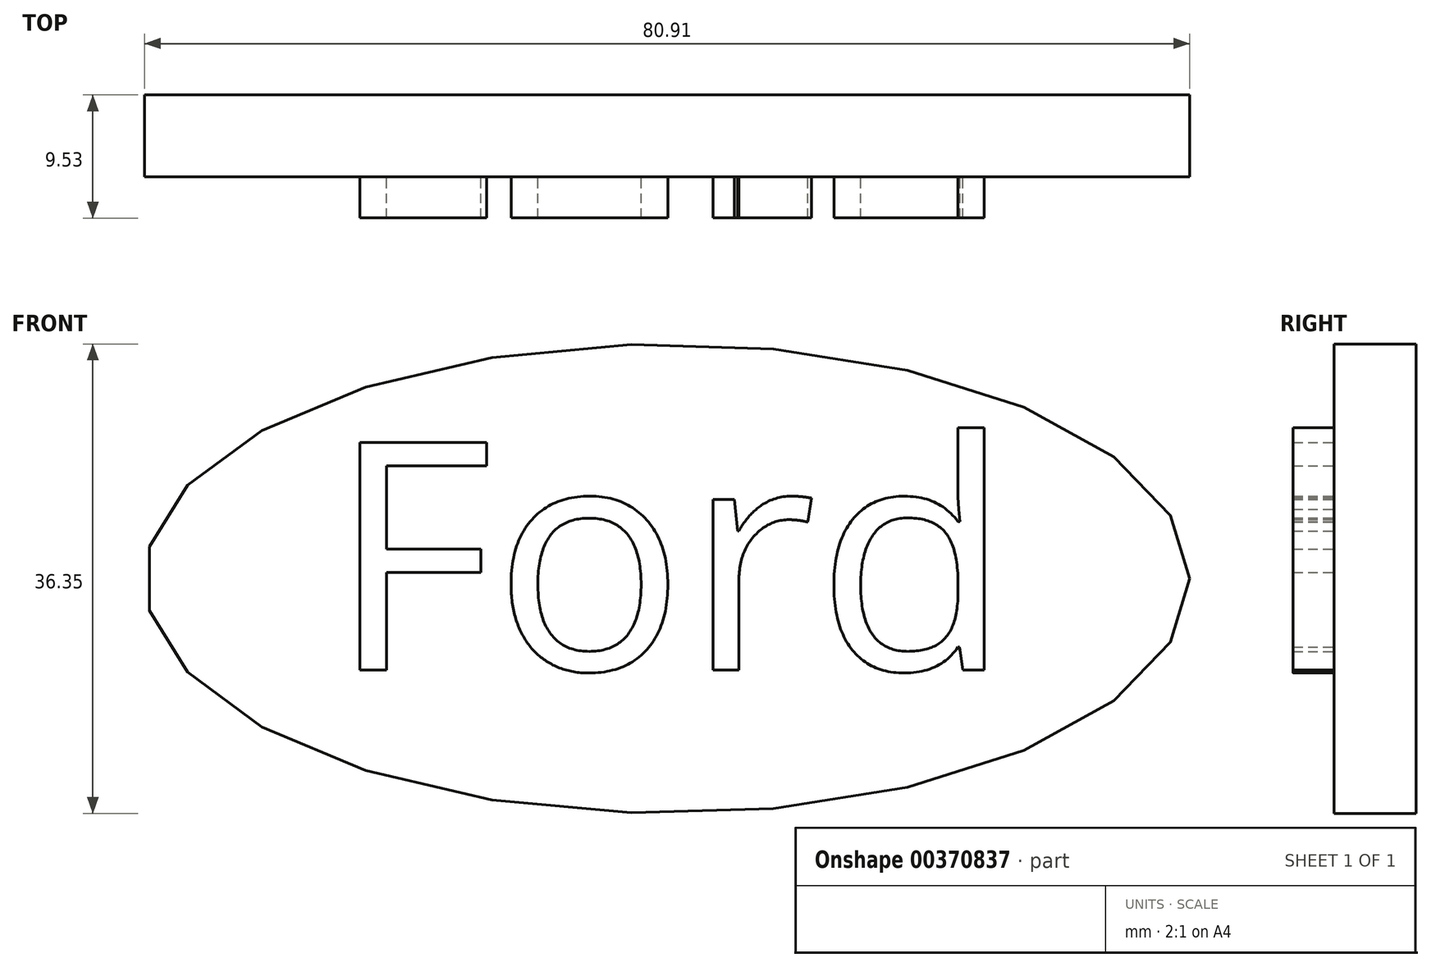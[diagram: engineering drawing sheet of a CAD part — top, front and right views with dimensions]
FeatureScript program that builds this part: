
annotation { "Feature Type Name" : "Feature", "Feature Type Description" : "" }
export const myFeature = defineFeature(function(context is Context, id is Id, definition is map)
    precondition{}
    {
        {
            var Q0;
            Q0=qCreatedBy(makeId("Front.planeOp"),FACE);
            var sketch = newSketch(context, id + "F0", { "sketchPlane" : qUnion([Q0])});
            skEllipse(sketch, "E0", {"center": v(-27.06, 23.06) * mm, "majorRadius": 40.46 * mm, "minorRadius": 18.17 * mm, "majorAxis": v(1, 0)});
            skSolve(sketch);
        }
        {
            var Q0;
            Q0 = qSketchRegion(id + "F0", true);
            extrude(context, id + "F1", {"entities" : qUnion([Q0]), "depth" : 6.35 * mm});
        }
        {
            var Q0;
            Q0=makeQuery(id+"F1.opExtrude","CAP_FACE",FACE,{"disambiguationData":[OSD([sQuery(id+"F0.wireOp",EDGE,"E0")])],"isStart":false});
            var sketch = newSketch(context, id + "F2", { "sketchPlane" : qUnion([Q0])});
            skText(sketch, "E1", { "text": "Ford", "fontName": "OpenSans-Regular.ttf"});
            const initialGuessF2  = {"E1": [-0.05326, 0.016, 1, 0, 0.01777]};
            skSetInitialGuess(sketch, initialGuessF2);
            skSolve(sketch);
        }
        {
            var Q0;
            Q0 = qSketchRegion(id + "F2", true);
            extrude(context, id + "F3", {"entities" : qUnion([Q0]), "operationType" : NewBodyOperationType.ADD, "depth" : 3.17 * mm});
        }
    });
